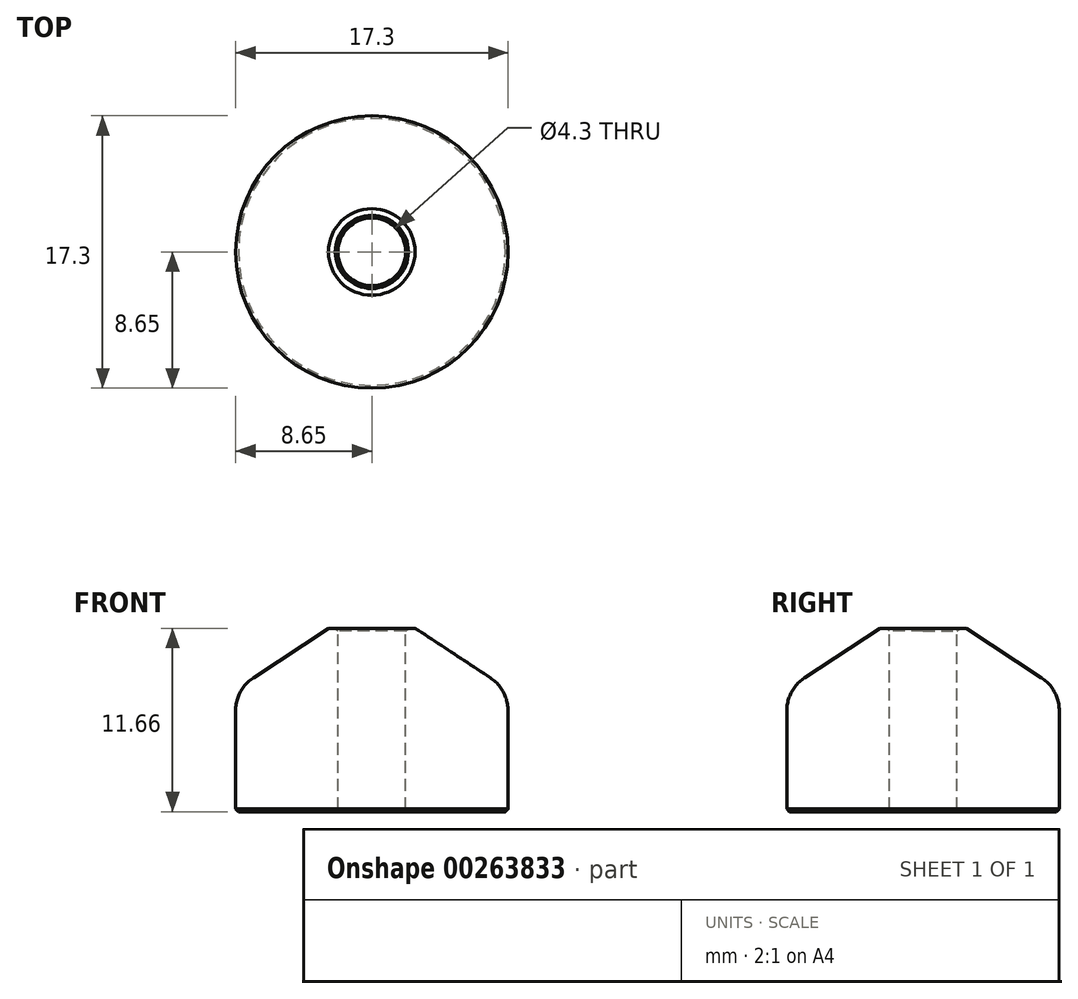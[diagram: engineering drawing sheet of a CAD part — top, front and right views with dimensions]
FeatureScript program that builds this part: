
annotation { "Feature Type Name" : "Feature", "Feature Type Description" : "" }
export const myFeature = defineFeature(function(context is Context, id is Id, definition is map)
    precondition{}
    {
        {
            var Q0;
            Q0=qCreatedBy(makeId("Right.planeOp"),FACE);
            var sketch = newSketch(context, id + "F0", { "sketchPlane" : qUnion([Q0])});
            skLineSegment(sketch, "E0", {"start": v(-8.65, 0) * mm, "end": v(-8.65, 7.77) * mm});
            skLineSegment(sketch, "E1", {"start": v(-2.15, 11.66) * mm, "end": v(-2.15, 0) * mm});
            skLineSegment(sketch, "E2", {"start": v(-2.15, 0) * mm, "end": v(-8.65, 0) * mm});
            skLineSegment(sketch, "E3", {"start": v(0, 17.21) * mm, "end": v(0, 0) * mm, "construction": true});
            skLineSegment(sketch, "E4", {"start": v(-8.65, 7.77) * mm, "end": v(-2.75, 11.66) * mm});
            skLineSegment(sketch, "E5", {"start": v(-2.75, 11.66) * mm, "end": v(-2.15, 11.66) * mm});
            skSolve(sketch);
        }
        {
            var Q0;
            Q0=qSketchRegion(id+"F0",true);
            var Q1;
            Q1=sQuery(id+"F0.wireOp",EDGE,"E3");
            revolve(context, id + "F1", {"entities" : qUnion([Q0]), "axis" : qUnion([Q1]), "revolveType" : RevolveType.FULL});
        }
        {
            var Q0;
            Q0=makeQuery(id+"F1.opRevolve","SWEPT_EDGE",EDGE,{"disambiguationData":[OSD([sQuery(id+"F0.wireOp",EDGE,"E1"),sQuery(id+"F0.wireOp",EDGE,"E5")])]});
            var Q1;
            Q1=makeQuery(id+"F1.opRevolve","SWEPT_EDGE",EDGE,{"disambiguationData":[OSD([sQuery(id+"F0.wireOp",EDGE,"E0"),sQuery(id+"F0.wireOp",EDGE,"E2")])]});
            var Q2;
            Q2=makeQuery(id+"F1.opRevolve","SWEPT_EDGE",EDGE,{"disambiguationData":[OSD([sQuery(id+"F0.wireOp",EDGE,"E1"),sQuery(id+"F0.wireOp",EDGE,"E2")])]});
            chamfer(context, id + "F2", {"entities" : qUnion([Q0, Q1, Q2]), "width" : .35 * mm / 2, "tangentPropagation" : true});
        }
        {
            var Q0;
            Q0=makeQuery(id+"F1.opRevolve","SWEPT_EDGE",EDGE,{"disambiguationData":[OSD([sQuery(id+"F0.wireOp",EDGE,"E0"),sQuery(id+"F0.wireOp",EDGE,"E4")])]});
            fillet(context, id + "F3", {"entities" : qUnion([Q0]), "radius" : 2.5 * mm, "tangentPropagation" : true, "allowEdgeOverflow" : false});
        }
    });
